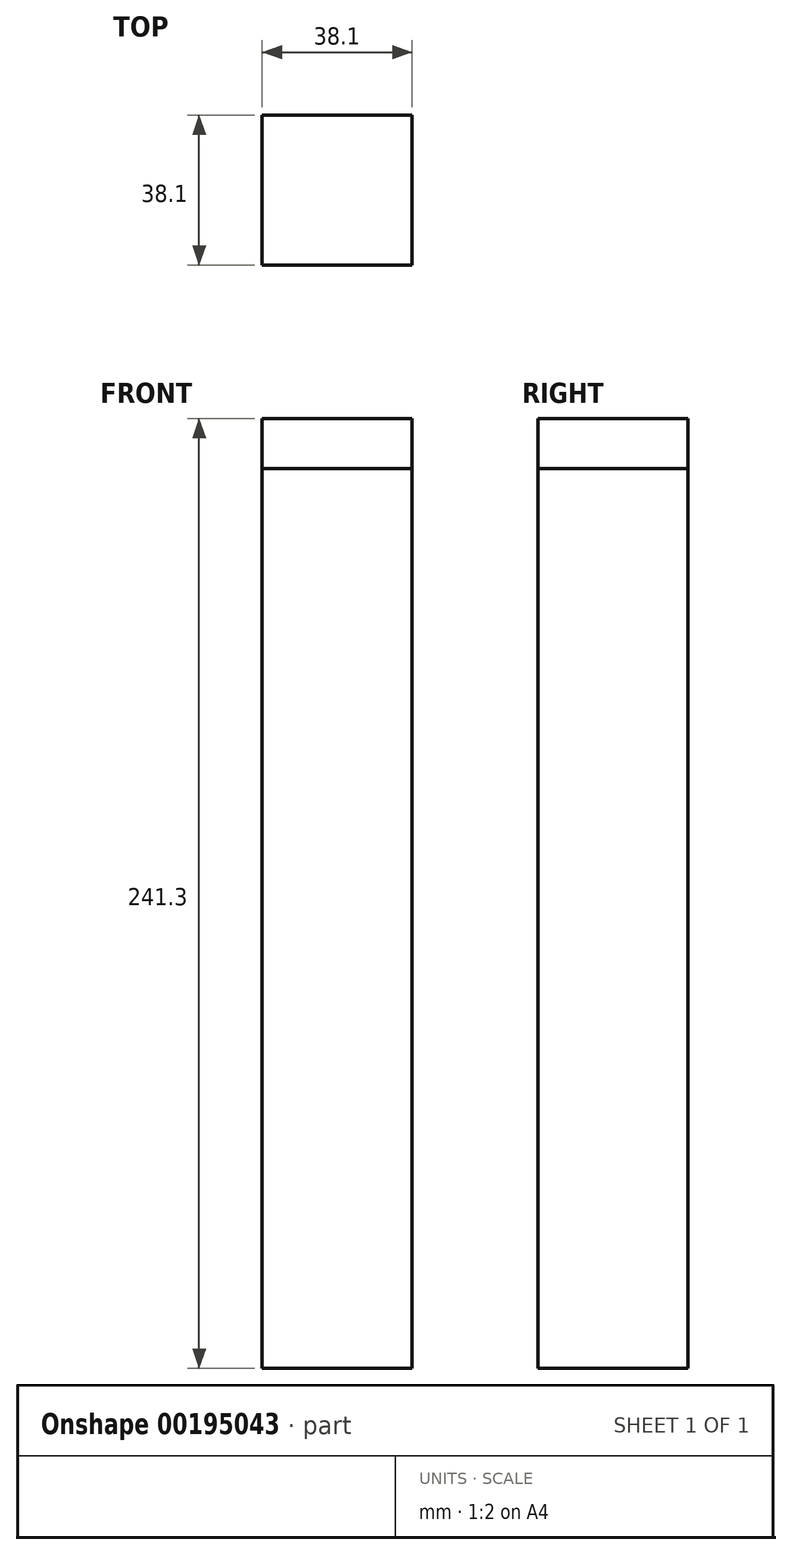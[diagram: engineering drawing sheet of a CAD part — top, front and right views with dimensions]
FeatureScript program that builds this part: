
annotation { "Feature Type Name" : "Feature", "Feature Type Description" : "" }
export const myFeature = defineFeature(function(context is Context, id is Id, definition is map)
    precondition{}
    {
        {
            var Q0;
            Q0=qCreatedBy(makeId("Top.planeOp"),FACE);
            var sketch = newSketch(context, id + "F0", { "sketchPlane" : qUnion([Q0])});
            skLineSegment(sketch, "E0.bottom", {"start": v(0, 0) * mm, "end": v(38.1, 0) * mm});
            skLineSegment(sketch, "E0.top", {"start": v(0, 38.1) * mm, "end": v(38.1, 38.1) * mm});
            skLineSegment(sketch, "E0.left", {"start": v(0, 0) * mm, "end": v(0, 38.1) * mm});
            skLineSegment(sketch, "E0.right", {"start": v(38.1, 0) * mm, "end": v(38.1, 38.1) * mm});
            skSolve(sketch);
        }
        {
            var Q0;
            Q0 = qSketchRegion(id + "F0", true);
            extrude(context, id + "F1", {"entities" : qUnion([Q0]), "depth" : 228.6 * mm});
        }
        {
            var Q0;
            Q0=makeQuery(id+"F1.opExtrude","CAP_FACE",FACE,{"disambiguationData":[OSD([sQuery(id+"F0.wireOp",EDGE,"E0.bottom"),sQuery(id+"F0.wireOp",EDGE,"E0.top"),sQuery(id+"F0.wireOp",EDGE,"E0.left"),sQuery(id+"F0.wireOp",EDGE,"E0.right")])],"isStart":false});
            cPlane(context, id + "F2", {"entities" : qUnion([Q0]), "cplaneType" : CPlaneType.OFFSET, "offset" : 0 * mm, "width" : 152.4 * mm, "height" : 152.4 * mm});
        }
        {
            var Q0;
            Q0=qCreatedBy(id+"F2.planeOp",FACE);
            var sketch = newSketch(context, id + "F3", { "sketchPlane" : qUnion([Q0])});
            skLineSegment(sketch, "E1.0.0", {"start": v(0, 38.1) * mm, "end": v(0, 0) * mm});
            skLineSegment(sketch, "E1.0.1", {"start": v(0, 0) * mm, "end": v(38.1, 0) * mm});
            skLineSegment(sketch, "E1.0.2", {"start": v(38.1, 0) * mm, "end": v(38.1, 38.1) * mm});
            skLineSegment(sketch, "E1.0.3", {"start": v(38.1, 38.1) * mm, "end": v(0, 38.1) * mm});
            skSolve(sketch);
        }
        {
            var Q0;
            Q0 = qSketchRegion(id + "F3", true);
            extrude(context, id + "F4", {"entities" : qUnion([Q0]), "depth" : 12.7 * mm});
        }
    });
